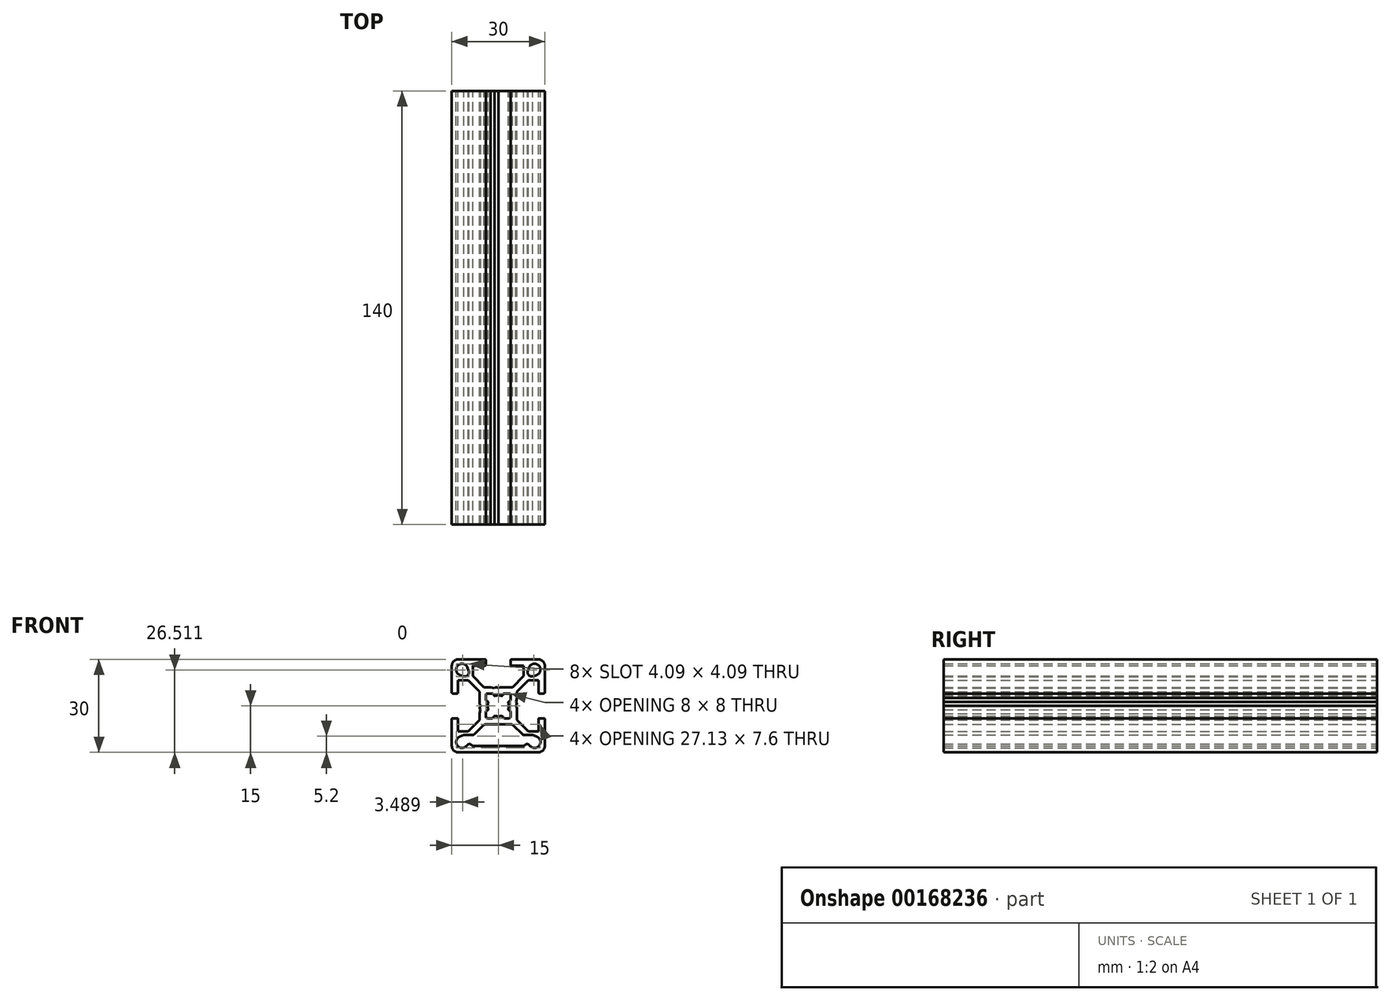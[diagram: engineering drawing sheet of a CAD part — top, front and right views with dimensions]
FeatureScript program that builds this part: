
annotation { "Feature Type Name" : "Feature", "Feature Type Description" : "" }
export const myFeature = defineFeature(function(context is Context, id is Id, definition is map)
    precondition{}
    {
        {
            var Q0;
            Q0=qCreatedBy(makeId("Front.planeOp"),FACE);
            var sketch = newSketch(context, id + "F0", { "sketchPlane" : qUnion([Q0])});
            skLineSegment(sketch, "E0", {"start": v(0, 17) * mm, "end": v(0, -17) * mm});
            skLineSegment(sketch, "E1", {"start": v(-17, 0) * mm, "end": v(17, 0) * mm});
            skLineSegment(sketch, "E2", {"start": v(-13, 15) * mm, "end": v(-4.3, 15) * mm});
            skLineSegment(sketch, "E3", {"start": v(-13, -15) * mm, "end": v(13, -15) * mm});
            skLineSegment(sketch, "E4", {"start": v(-15, 13) * mm, "end": v(-15, 4.3) * mm});
            skArc(sketch, "E5", {"start": v(15, 13) * mm, "mid": v(14.41, 14.41) * mm, "end": v(13, 15) * mm});
            skArc(sketch, "E6", {"start": v(-13, 15) * mm, "mid": v(-14.41, 14.41) * mm, "end": v(-15, 13) * mm});
            skArc(sketch, "E7", {"start": v(-15, -13) * mm, "mid": v(-14.41, -14.41) * mm, "end": v(-13, -15) * mm});
            skArc(sketch, "E8", {"start": v(13, -15) * mm, "mid": v(14.41, -14.41) * mm, "end": v(15, -13) * mm});
            skLineSegment(sketch, "E9", {"start": v(-13, -8.25) * mm, "end": v(-13, -4.3) * mm});
            skLineSegment(sketch, "E10", {"start": v(-8.08, -13) * mm, "end": v(8.08, -13) * mm});
            skLineSegment(sketch, "E11", {"start": v(-14.7, -4) * mm, "end": v(-13.3, -4) * mm});
            skLineSegment(sketch, "E12", {"start": v(-14.7, 4) * mm, "end": v(-13.3, 4) * mm});
            skLineSegment(sketch, "E13", {"start": v(-13, 4.3) * mm, "end": v(-13, 8.25) * mm});
            skLineSegment(sketch, "E14", {"start": v(4.3, 15) * mm, "end": v(13, 15) * mm});
            skLineSegment(sketch, "E15", {"start": v(-9.66, -8.25) * mm, "end": v(-13, -8.25) * mm});
            skLineSegment(sketch, "E16", {"start": v(-9.66, 8.25) * mm, "end": v(-13, 8.25) * mm});
            skLineSegment(sketch, "E17", {"start": v(4.59, 6) * mm, "end": v(0.65, 6) * mm});
            skLineSegment(sketch, "E18", {"start": v(4.17, -6) * mm, "end": v(-4.17, -6) * mm});
            skLineSegment(sketch, "E19", {"start": v(-6, -4.59) * mm, "end": v(-6, -2.5) * mm});
            skLineSegment(sketch, "E20", {"start": v(-4.59, 6) * mm, "end": v(-8.25, 9.66) * mm});
            skLineSegment(sketch, "E21", {"start": v(-6, 4.59) * mm, "end": v(-9.66, 8.25) * mm});
            skLineSegment(sketch, "E22", {"start": v(4.59, 6) * mm, "end": v(8.25, 9.66) * mm});
            skLineSegment(sketch, "E23", {"start": v(4.88, -6.3) * mm, "end": v(7.74, -9.16) * mm});
            skLineSegment(sketch, "E24", {"start": v(-4.88, -6.3) * mm, "end": v(-7.74, -9.16) * mm});
            skLineSegment(sketch, "E25", {"start": v(-6, -4.59) * mm, "end": v(-9.66, -8.25) * mm});
            skLineSegment(sketch, "E26", {"start": v(-15, -4.3) * mm, "end": v(-15, -13) * mm});
            skLineSegment(sketch, "E27", {"start": v(-4, 14.7) * mm, "end": v(-4, 13.3) * mm});
            skLineSegment(sketch, "E28", {"start": v(4, 14.7) * mm, "end": v(4, 13.3) * mm});
            skLineSegment(sketch, "E29", {"start": v(8.25, 9.66) * mm, "end": v(8.25, 13) * mm});
            skLineSegment(sketch, "E30", {"start": v(-8.25, 9.66) * mm, "end": v(-8.25, 13) * mm});
            skLineSegment(sketch, "E31", {"start": v(-4.3, 13) * mm, "end": v(-8.25, 13) * mm});
            skLineSegment(sketch, "E32", {"start": v(4.3, 13) * mm, "end": v(8.25, 13) * mm});
            skArc(sketch, "E33", {"start": v(-9.91, 12.35) * mm, "mid": v(-13.04, 13.04) * mm, "end": v(-12.35, 9.91) * mm});
            skLineSegment(sketch, "E34", {"start": v(-9.55, 11.34) * mm, "end": v(-9.91, 12.35) * mm});
            skLineSegment(sketch, "E35", {"start": v(-11.34, 9.55) * mm, "end": v(-12.35, 9.91) * mm});
            skArc(sketch, "E36", {"start": v(-11.34, 9.55) * mm, "mid": v(-9.87, 9.87) * mm, "end": v(-9.55, 11.34) * mm});
            skLineSegment(sketch, "E37", {"start": v(-8.45, -9.45) * mm, "end": v(-11.07, -9.45) * mm});
            skLineSegment(sketch, "E38", {"start": v(-11.07, -9.45) * mm, "end": v(-12.35, -9.91) * mm});
            skArc(sketch, "E39", {"start": v(-12.35, -9.91) * mm, "mid": v(-13.2, -12.86) * mm, "end": v(-10.14, -12.78) * mm});
            skArc(sketch, "E40", {"start": v(-8.5, -12.78) * mm, "mid": v(-9.31, -12.35) * mm, "end": v(-10.14, -12.78) * mm});
            skArc(sketch, "E41", {"start": v(-8.45, -9.45) * mm, "mid": v(-8.07, -9.37) * mm, "end": v(-7.74, -9.16) * mm});
            skArc(sketch, "E42", {"start": v(-4.17, -6) * mm, "mid": v(-4.55, -6.08) * mm, "end": v(-4.88, -6.3) * mm});
            skArc(sketch, "E43", {"start": v(4.88, -6.3) * mm, "mid": v(4.55, -6.08) * mm, "end": v(4.17, -6) * mm});
            skLineSegment(sketch, "E44", {"start": v(3.5, 4) * mm, "end": v(2, 4) * mm});
            skLineSegment(sketch, "E45", {"start": v(4, -3.5) * mm, "end": v(4, -2) * mm});
            skLineSegment(sketch, "E46", {"start": v(3.5, -4) * mm, "end": v(2, -4) * mm});
            skLineSegment(sketch, "E47", {"start": v(-4, -3.5) * mm, "end": v(-4, -2) * mm});
            skLineSegment(sketch, "E48", {"start": v(-2.5, 6) * mm, "end": v(-1.22, 5.75) * mm});
            skLineSegment(sketch, "E49", {"start": v(0, 5.7) * mm, "end": v(-0.4, 5.93) * mm});
            skLineSegment(sketch, "E50", {"start": v(0, 5.7) * mm, "end": v(0.4, 5.93) * mm});
            skLineSegment(sketch, "E51", {"start": v(-2.5, 6) * mm, "end": v(-4.59, 6) * mm});
            skArc(sketch, "E52", {"start": v(0.65, 6) * mm, "mid": v(0.52, 5.98) * mm, "end": v(0.4, 5.93) * mm});
            skArc(sketch, "E53", {"start": v(-0.4, 5.93) * mm, "mid": v(-0.65, 6) * mm, "end": v(-0.9, 5.93) * mm});
            skLineSegment(sketch, "E54", {"start": v(-1.22, 5.75) * mm, "end": v(-0.9, 5.93) * mm});
            skArc(sketch, "E55", {"start": v(-6, 0.65) * mm, "mid": v(-5.98, 0.52) * mm, "end": v(-5.93, 0.4) * mm});
            skLineSegment(sketch, "E56", {"start": v(-6, -2.5) * mm, "end": v(-5.75, -1.22) * mm});
            skLineSegment(sketch, "E57", {"start": v(-5.7, 0) * mm, "end": v(-5.93, -0.4) * mm});
            skLineSegment(sketch, "E58", {"start": v(-5.7, 0) * mm, "end": v(-5.93, 0.4) * mm});
            skArc(sketch, "E59", {"start": v(-5.93, -0.4) * mm, "mid": v(-6, -0.65) * mm, "end": v(-5.93, -0.9) * mm});
            skLineSegment(sketch, "E60", {"start": v(-5.75, -1.22) * mm, "end": v(-5.93, -0.9) * mm});
            skLineSegment(sketch, "E61", {"start": v(-6, 0.65) * mm, "end": v(-6, 4.59) * mm});
            skArc(sketch, "E62", {"start": v(4, 13.3) * mm, "mid": v(4.09, 13.09) * mm, "end": v(4.3, 13) * mm});
            skArc(sketch, "E63", {"start": v(4.3, 15) * mm, "mid": v(4.09, 14.91) * mm, "end": v(4, 14.7) * mm});
            skArc(sketch, "E64", {"start": v(-4.3, 13) * mm, "mid": v(-4.09, 13.09) * mm, "end": v(-4, 13.3) * mm});
            skArc(sketch, "E65", {"start": v(-4, 14.7) * mm, "mid": v(-4.09, 14.91) * mm, "end": v(-4.3, 15) * mm});
            skArc(sketch, "E66", {"start": v(-13.3, 4) * mm, "mid": v(-13.09, 4.09) * mm, "end": v(-13, 4.3) * mm});
            skArc(sketch, "E67", {"start": v(-15, 4.3) * mm, "mid": v(-14.91, 4.09) * mm, "end": v(-14.7, 4) * mm});
            skArc(sketch, "E68", {"start": v(-13, -4.3) * mm, "mid": v(-13.09, -4.09) * mm, "end": v(-13.3, -4) * mm});
            skArc(sketch, "E69", {"start": v(-14.7, -4) * mm, "mid": v(-14.91, -4.09) * mm, "end": v(-15, -4.3) * mm});
            skArc(sketch, "E70", {"start": v(0.99, 3.25) * mm, "mid": v(0, 3.4) * mm, "end": v(-0.99, 3.25) * mm});
            skArc(sketch, "E71", {"start": v(-1.5, 3.58) * mm, "mid": v(-1.32, 3.3) * mm, "end": v(-0.99, 3.25) * mm});
            skArc(sketch, "E72", {"start": v(-1.5, 3.58) * mm, "mid": v(-1.67, 3.88) * mm, "end": v(-2, 4) * mm});
            skArc(sketch, "E73", {"start": v(0.99, 3.25) * mm, "mid": v(1.32, 3.3) * mm, "end": v(1.5, 3.58) * mm});
            skArc(sketch, "E74", {"start": v(2, 4) * mm, "mid": v(1.67, 3.88) * mm, "end": v(1.5, 3.58) * mm});
            skLineSegment(sketch, "E75", {"start": v(-2, 4) * mm, "end": v(-3.5, 4) * mm});
            skArc(sketch, "E76", {"start": v(-3.5, 4) * mm, "mid": v(-3.85, 3.85) * mm, "end": v(-4, 3.5) * mm});
            skArc(sketch, "E77", {"start": v(4, 3.5) * mm, "mid": v(3.85, 3.85) * mm, "end": v(3.5, 4) * mm});
            skArc(sketch, "E78", {"start": v(3.5, -4) * mm, "mid": v(3.85, -3.85) * mm, "end": v(4, -3.5) * mm});
            skArc(sketch, "E79", {"start": v(-4, -3.5) * mm, "mid": v(-3.85, -3.85) * mm, "end": v(-3.5, -4) * mm});
            skArc(sketch, "E80", {"start": v(-3.25, 0.99) * mm, "mid": v(-3.4, 0) * mm, "end": v(-3.25, -0.99) * mm});
            skArc(sketch, "E81", {"start": v(-3.58, -1.5) * mm, "mid": v(-3.3, -1.32) * mm, "end": v(-3.25, -0.99) * mm});
            skArc(sketch, "E82", {"start": v(-3.58, -1.5) * mm, "mid": v(-3.88, -1.67) * mm, "end": v(-4, -2) * mm});
            skArc(sketch, "E83", {"start": v(-3.25, 0.99) * mm, "mid": v(-3.3, 1.32) * mm, "end": v(-3.58, 1.5) * mm});
            skArc(sketch, "E84", {"start": v(-4, 2) * mm, "mid": v(-3.88, 1.67) * mm, "end": v(-3.58, 1.5) * mm});
            skArc(sketch, "E85", {"start": v(3.25, -0.99) * mm, "mid": v(3.4, 0) * mm, "end": v(3.25, 0.99) * mm});
            skArc(sketch, "E86", {"start": v(3.58, 1.5) * mm, "mid": v(3.3, 1.32) * mm, "end": v(3.25, 0.99) * mm});
            skArc(sketch, "E87", {"start": v(3.58, 1.5) * mm, "mid": v(3.88, 1.67) * mm, "end": v(4, 2) * mm});
            skArc(sketch, "E88", {"start": v(3.25, -0.99) * mm, "mid": v(3.3, -1.32) * mm, "end": v(3.58, -1.5) * mm});
            skArc(sketch, "E89", {"start": v(4, -2) * mm, "mid": v(3.88, -1.67) * mm, "end": v(3.58, -1.5) * mm});
            skArc(sketch, "E90", {"start": v(-0.99, -3.25) * mm, "mid": v(0, -3.4) * mm, "end": v(0.99, -3.25) * mm});
            skArc(sketch, "E91", {"start": v(-0.99, -3.25) * mm, "mid": v(-1.32, -3.3) * mm, "end": v(-1.5, -3.58) * mm});
            skArc(sketch, "E92", {"start": v(-2, -4) * mm, "mid": v(-1.67, -3.88) * mm, "end": v(-1.5, -3.58) * mm});
            skArc(sketch, "E93", {"start": v(1.5, -3.58) * mm, "mid": v(1.32, -3.3) * mm, "end": v(0.99, -3.25) * mm});
            skArc(sketch, "E94", {"start": v(1.5, -3.58) * mm, "mid": v(1.67, -3.88) * mm, "end": v(2, -4) * mm});
            skLineSegment(sketch, "E95", {"start": v(4, 2) * mm, "end": v(4, 3.5) * mm});
            skLineSegment(sketch, "E96", {"start": v(-2, -4) * mm, "end": v(-3.5, -4) * mm});
            skLineSegment(sketch, "E97", {"start": v(-4, 2) * mm, "end": v(-4, 3.5) * mm});
            skCircle(sketch, "E98", {"center": v(0, 0) * mm, "radius": 3.4 * mm});
            skLineSegment(sketch, "E99", {"start": v(-11.7, -7.8) * mm, "end": v(-11.7, -15.6) * mm});
            skLineSegment(sketch, "E100", {"start": v(-15.6, -11.7) * mm, "end": v(-7.8, -11.7) * mm});
            skLineSegment(sketch, "E101", {"start": v(-11.7, 15.6) * mm, "end": v(-11.7, 7.8) * mm});
            skLineSegment(sketch, "E102", {"start": v(-15.6, 11.7) * mm, "end": v(-7.8, 11.7) * mm});
            skArc(sketch, "E103", {"start": v(7.74, -9.16) * mm, "mid": v(8.07, -9.37) * mm, "end": v(8.45, -9.45) * mm});
            skArc(sketch, "E104", {"start": v(12.35, 9.91) * mm, "mid": v(13.04, 13.04) * mm, "end": v(9.91, 12.35) * mm});
            skLineSegment(sketch, "E105", {"start": v(9.55, 11.34) * mm, "end": v(9.91, 12.35) * mm});
            skLineSegment(sketch, "E106", {"start": v(11.34, 9.55) * mm, "end": v(12.35, 9.91) * mm});
            skArc(sketch, "E107", {"start": v(9.55, 11.34) * mm, "mid": v(9.87, 9.87) * mm, "end": v(11.34, 9.55) * mm});
            skLineSegment(sketch, "E108", {"start": v(8.45, -9.45) * mm, "end": v(11.07, -9.45) * mm});
            skLineSegment(sketch, "E109", {"start": v(11.07, -9.45) * mm, "end": v(12.35, -9.91) * mm});
            skArc(sketch, "E110", {"start": v(10.14, -12.78) * mm, "mid": v(13.2, -12.86) * mm, "end": v(12.35, -9.91) * mm});
            skArc(sketch, "E111", {"start": v(10.14, -12.78) * mm, "mid": v(9.31, -12.35) * mm, "end": v(8.5, -12.78) * mm});
            skLineSegment(sketch, "E112", {"start": v(11.7, -7.8) * mm, "end": v(11.7, -15.6) * mm});
            skLineSegment(sketch, "E113", {"start": v(15.6, -11.7) * mm, "end": v(7.8, -11.7) * mm});
            skLineSegment(sketch, "E114", {"start": v(11.7, 15.6) * mm, "end": v(11.7, 7.8) * mm});
            skLineSegment(sketch, "E115", {"start": v(15.6, 11.7) * mm, "end": v(7.8, 11.7) * mm});
            skLineSegment(sketch, "E116", {"start": v(15, 13) * mm, "end": v(15, 4.3) * mm});
            skLineSegment(sketch, "E117", {"start": v(15, -4.3) * mm, "end": v(15, -13) * mm});
            skLineSegment(sketch, "E118", {"start": v(13, -8.25) * mm, "end": v(13, -4.3) * mm});
            skLineSegment(sketch, "E119", {"start": v(13, 4.3) * mm, "end": v(13, 8.25) * mm});
            skLineSegment(sketch, "E120", {"start": v(14.7, -4) * mm, "end": v(13.3, -4) * mm});
            skArc(sketch, "E121", {"start": v(13.3, -4) * mm, "mid": v(13.09, -4.09) * mm, "end": v(13, -4.3) * mm});
            skLineSegment(sketch, "E122", {"start": v(14.7, 4) * mm, "end": v(13.3, 4) * mm});
            skArc(sketch, "E123", {"start": v(14.7, 4) * mm, "mid": v(14.91, 4.09) * mm, "end": v(15, 4.3) * mm});
            skArc(sketch, "E124", {"start": v(13, 4.3) * mm, "mid": v(13.09, 4.09) * mm, "end": v(13.3, 4) * mm});
            skLineSegment(sketch, "E125", {"start": v(9.66, 8.25) * mm, "end": v(13, 8.25) * mm});
            skLineSegment(sketch, "E126", {"start": v(9.66, -8.25) * mm, "end": v(13, -8.25) * mm});
            skLineSegment(sketch, "E127", {"start": v(6, 4.59) * mm, "end": v(9.66, 8.25) * mm});
            skLineSegment(sketch, "E128", {"start": v(6, -4.59) * mm, "end": v(9.66, -8.25) * mm});
            skArc(sketch, "E129", {"start": v(15, -4.3) * mm, "mid": v(14.91, -4.09) * mm, "end": v(14.7, -4) * mm});
            skLineSegment(sketch, "E130", {"start": v(6, 4.59) * mm, "end": v(6, 2.5) * mm});
            skLineSegment(sketch, "E131", {"start": v(6, -0.65) * mm, "end": v(6, -4.59) * mm});
            skArc(sketch, "E132", {"start": v(6, -0.65) * mm, "mid": v(5.98, -0.52) * mm, "end": v(5.93, -0.4) * mm});
            skLineSegment(sketch, "E133", {"start": v(6, 2.5) * mm, "end": v(5.75, 1.22) * mm});
            skLineSegment(sketch, "E134", {"start": v(5.7, 0) * mm, "end": v(5.93, 0.4) * mm});
            skLineSegment(sketch, "E135", {"start": v(5.7, 0) * mm, "end": v(5.93, -0.4) * mm});
            skArc(sketch, "E136", {"start": v(5.93, 0.4) * mm, "mid": v(6, 0.65) * mm, "end": v(5.93, 0.9) * mm});
            skLineSegment(sketch, "E137", {"start": v(5.75, 1.22) * mm, "end": v(5.93, 0.9) * mm});
            skArc(sketch, "E138", {"start": v(8.08, -13) * mm, "mid": v(8.31, -12.94) * mm, "end": v(8.5, -12.78) * mm});
            skArc(sketch, "E139", {"start": v(-8.5, -12.78) * mm, "mid": v(-8.31, -12.94) * mm, "end": v(-8.08, -13) * mm});
            skSolve(sketch);
        }
        {
            var Q0;
            Q0=qCreatedBy(makeId("Front.planeOp"),FACE);
            var sketch = newSketch(context, id + "F1", { "sketchPlane" : qUnion([Q0])});
            skLineSegment(sketch, "E140.0", {"start": v(4.59, 6) * mm, "end": v(0.65, 6) * mm});
            skLineSegment(sketch, "E140.2", {"start": v(6, 4.59) * mm, "end": v(6, 2.5) * mm});
            skLineSegment(sketch, "E140.5", {"start": v(6, -0.65) * mm, "end": v(6, -4.59) * mm});
            skLineSegment(sketch, "E140.7", {"start": v(4.3, 13) * mm, "end": v(8.25, 13) * mm});
            skLineSegment(sketch, "E140.8", {"start": v(-15, 13) * mm, "end": v(-15, 4.3) * mm});
            skLineSegment(sketch, "E140.11", {"start": v(6, -4.59) * mm, "end": v(9.66, -8.25) * mm});
            skArc(sketch, "E140.12", {"start": v(-9.91, 12.35) * mm, "mid": v(-13.04, 13.04) * mm, "end": v(-12.35, 9.91) * mm});
            skLineSegment(sketch, "E140.13", {"start": v(4.17, -6) * mm, "end": v(-4.17, -6) * mm});
            skLineSegment(sketch, "E140.14", {"start": v(-2.5, 6) * mm, "end": v(-4.59, 6) * mm});
            skArc(sketch, "E140.15", {"start": v(15, 13) * mm, "mid": v(14.41, 14.41) * mm, "end": v(13, 15) * mm});
            skLineSegment(sketch, "E140.16", {"start": v(-8.08, -13) * mm, "end": v(8.08, -13) * mm});
            skLineSegment(sketch, "E140.17", {"start": v(-13, -8.25) * mm, "end": v(-13, -4.3) * mm});
            skArc(sketch, "E140.18", {"start": v(-15, -13) * mm, "mid": v(-14.41, -14.41) * mm, "end": v(-13, -15) * mm});
            skArc(sketch, "E140.19", {"start": v(13, -15) * mm, "mid": v(14.41, -14.41) * mm, "end": v(15, -13) * mm});
            skArc(sketch, "E140.20", {"start": v(-13, 15) * mm, "mid": v(-14.41, 14.41) * mm, "end": v(-15, 13) * mm});
            skLineSegment(sketch, "E140.21", {"start": v(15, 13) * mm, "end": v(15, 4.3) * mm});
            skLineSegment(sketch, "E140.22", {"start": v(-13, 15) * mm, "end": v(-4.3, 15) * mm});
            skLineSegment(sketch, "E140.23", {"start": v(-13, -15) * mm, "end": v(13, -15) * mm});
            skLineSegment(sketch, "E140.26", {"start": v(-9.66, -8.25) * mm, "end": v(-13, -8.25) * mm});
            skLineSegment(sketch, "E140.27", {"start": v(4.3, 15) * mm, "end": v(13, 15) * mm});
            skLineSegment(sketch, "E140.28", {"start": v(-4.3, 13) * mm, "end": v(-8.25, 13) * mm});
            skLineSegment(sketch, "E140.29", {"start": v(6, 4.59) * mm, "end": v(9.66, 8.25) * mm});
            skLineSegment(sketch, "E140.30", {"start": v(-13, 4.3) * mm, "end": v(-13, 8.25) * mm});
            skLineSegment(sketch, "E140.31", {"start": v(-6, -4.59) * mm, "end": v(-6, -2.5) * mm});
            skArc(sketch, "E140.32", {"start": v(-11.34, 9.55) * mm, "mid": v(-9.87, 9.87) * mm, "end": v(-9.55, 11.34) * mm});
            skArc(sketch, "E140.33", {"start": v(10.14, -12.78) * mm, "mid": v(13.2, -12.86) * mm, "end": v(12.35, -9.91) * mm});
            skLineSegment(sketch, "E140.34", {"start": v(8.45, -9.45) * mm, "end": v(11.07, -9.45) * mm});
            skLineSegment(sketch, "E140.35", {"start": v(-8.25, 9.66) * mm, "end": v(-8.25, 13) * mm});
            skLineSegment(sketch, "E140.36", {"start": v(9.66, -8.25) * mm, "end": v(13, -8.25) * mm});
            skLineSegment(sketch, "E140.37", {"start": v(8.25, 9.66) * mm, "end": v(8.25, 13) * mm});
            skLineSegment(sketch, "E140.38", {"start": v(-6, 0.65) * mm, "end": v(-6, 4.59) * mm});
            skArc(sketch, "E140.39", {"start": v(9.55, 11.34) * mm, "mid": v(9.87, 9.87) * mm, "end": v(11.34, 9.55) * mm});
            skLineSegment(sketch, "E140.40", {"start": v(9.66, 8.25) * mm, "end": v(13, 8.25) * mm});
            skLineSegment(sketch, "E140.41", {"start": v(-4.59, 6) * mm, "end": v(-8.25, 9.66) * mm});
            skLineSegment(sketch, "E140.42", {"start": v(-15, -4.3) * mm, "end": v(-15, -13) * mm});
            skLineSegment(sketch, "E140.43", {"start": v(-6, -4.59) * mm, "end": v(-9.66, -8.25) * mm});
            skArc(sketch, "E140.44", {"start": v(12.35, 9.91) * mm, "mid": v(13.04, 13.04) * mm, "end": v(9.91, 12.35) * mm});
            skLineSegment(sketch, "E140.45", {"start": v(-4.88, -6.3) * mm, "end": v(-7.74, -9.16) * mm});
            skLineSegment(sketch, "E140.46", {"start": v(13, -8.25) * mm, "end": v(13, -4.3) * mm});
            skArc(sketch, "E140.48", {"start": v(-12.35, -9.91) * mm, "mid": v(-13.2, -12.86) * mm, "end": v(-10.14, -12.78) * mm});
            skLineSegment(sketch, "E140.49", {"start": v(13, 4.3) * mm, "end": v(13, 8.25) * mm});
            skLineSegment(sketch, "E140.50", {"start": v(4.88, -6.3) * mm, "end": v(7.74, -9.16) * mm});
            skLineSegment(sketch, "E140.51", {"start": v(4.59, 6) * mm, "end": v(8.25, 9.66) * mm});
            skLineSegment(sketch, "E140.52", {"start": v(-8.45, -9.45) * mm, "end": v(-11.07, -9.45) * mm});
            skLineSegment(sketch, "E140.53", {"start": v(-6, 4.59) * mm, "end": v(-9.66, 8.25) * mm});
            skLineSegment(sketch, "E140.54", {"start": v(15, -4.3) * mm, "end": v(15, -13) * mm});
            skLineSegment(sketch, "E140.57", {"start": v(-9.66, 8.25) * mm, "end": v(-13, 8.25) * mm});
            skArc(sketch, "E140.58", {"start": v(-0.99, -3.25) * mm, "mid": v(0, -3.4) * mm, "end": v(0.99, -3.25) * mm});
            skArc(sketch, "E140.59", {"start": v(0.99, 3.25) * mm, "mid": v(0, 3.4) * mm, "end": v(-0.99, 3.25) * mm});
            skLineSegment(sketch, "E140.60", {"start": v(-11.34, 9.55) * mm, "end": v(-12.35, 9.91) * mm});
            skArc(sketch, "E140.61", {"start": v(-3.58, -1.5) * mm, "mid": v(-3.3, -1.32) * mm, "end": v(-3.25, -0.99) * mm});
            skLineSegment(sketch, "E140.62", {"start": v(-9.55, 11.34) * mm, "end": v(-9.91, 12.35) * mm});
            skLineSegment(sketch, "E140.63", {"start": v(-2.5, 6) * mm, "end": v(-1.22, 5.75) * mm});
            skLineSegment(sketch, "E140.64", {"start": v(-2, -4) * mm, "end": v(-3.5, -4) * mm});
            skLineSegment(sketch, "E140.65", {"start": v(-4, 2) * mm, "end": v(-4, 3.5) * mm});
            skArc(sketch, "E140.66", {"start": v(-3.25, 0.99) * mm, "mid": v(-3.4, 0) * mm, "end": v(-3.25, -0.99) * mm});
            skArc(sketch, "E140.67", {"start": v(-3.58, -1.5) * mm, "mid": v(-3.88, -1.67) * mm, "end": v(-4, -2) * mm});
            skLineSegment(sketch, "E140.68", {"start": v(4, 2) * mm, "end": v(4, 3.5) * mm});
            skArc(sketch, "E140.69", {"start": v(6, -0.65) * mm, "mid": v(5.98, -0.52) * mm, "end": v(5.93, -0.4) * mm});
            skArc(sketch, "E140.70", {"start": v(10.14, -12.78) * mm, "mid": v(9.31, -12.35) * mm, "end": v(8.5, -12.78) * mm});
            skArc(sketch, "E140.71", {"start": v(-4, -3.5) * mm, "mid": v(-3.85, -3.85) * mm, "end": v(-3.5, -4) * mm});
            skLineSegment(sketch, "E140.72", {"start": v(-4, -3.5) * mm, "end": v(-4, -2) * mm});
            skArc(sketch, "E140.73", {"start": v(1.5, -3.58) * mm, "mid": v(1.67, -3.88) * mm, "end": v(2, -4) * mm});
            skLineSegment(sketch, "E140.74", {"start": v(3.5, 4) * mm, "end": v(2, 4) * mm});
            skLineSegment(sketch, "E140.75", {"start": v(3.5, -4) * mm, "end": v(2, -4) * mm});
            skArc(sketch, "E140.76", {"start": v(3.5, -4) * mm, "mid": v(3.85, -3.85) * mm, "end": v(4, -3.5) * mm});
            skArc(sketch, "E140.77", {"start": v(-3.5, 4) * mm, "mid": v(-3.85, 3.85) * mm, "end": v(-4, 3.5) * mm});
            skLineSegment(sketch, "E140.78", {"start": v(4, -3.5) * mm, "end": v(4, -2) * mm});
            skArc(sketch, "E140.79", {"start": v(4, 3.5) * mm, "mid": v(3.85, 3.85) * mm, "end": v(3.5, 4) * mm});
            skLineSegment(sketch, "E140.80", {"start": v(-2, 4) * mm, "end": v(-3.5, 4) * mm});
            skArc(sketch, "E140.81", {"start": v(-8.5, -12.78) * mm, "mid": v(-8.31, -12.94) * mm, "end": v(-8.08, -13) * mm});
            skLineSegment(sketch, "E140.82", {"start": v(11.07, -9.45) * mm, "end": v(12.35, -9.91) * mm});
            skArc(sketch, "E140.83", {"start": v(4.88, -6.3) * mm, "mid": v(4.55, -6.08) * mm, "end": v(4.17, -6) * mm});
            skArc(sketch, "E140.84", {"start": v(8.08, -13) * mm, "mid": v(8.31, -12.94) * mm, "end": v(8.5, -12.78) * mm});
            skArc(sketch, "E140.85", {"start": v(-4, 2) * mm, "mid": v(-3.88, 1.67) * mm, "end": v(-3.58, 1.5) * mm});
            skArc(sketch, "E140.86", {"start": v(-4.17, -6) * mm, "mid": v(-4.55, -6.08) * mm, "end": v(-4.88, -6.3) * mm});
            skLineSegment(sketch, "E140.87", {"start": v(11.34, 9.55) * mm, "end": v(12.35, 9.91) * mm});
            skArc(sketch, "E140.88", {"start": v(-8.45, -9.45) * mm, "mid": v(-8.07, -9.37) * mm, "end": v(-7.74, -9.16) * mm});
            skLineSegment(sketch, "E140.89", {"start": v(9.55, 11.34) * mm, "end": v(9.91, 12.35) * mm});
            skArc(sketch, "E140.90", {"start": v(4, -2) * mm, "mid": v(3.88, -1.67) * mm, "end": v(3.58, -1.5) * mm});
            skArc(sketch, "E140.91", {"start": v(-1.5, 3.58) * mm, "mid": v(-1.67, 3.88) * mm, "end": v(-2, 4) * mm});
            skArc(sketch, "E140.92", {"start": v(-8.5, -12.78) * mm, "mid": v(-9.31, -12.35) * mm, "end": v(-10.14, -12.78) * mm});
            skArc(sketch, "E140.93", {"start": v(3.25, -0.99) * mm, "mid": v(3.3, -1.32) * mm, "end": v(3.58, -1.5) * mm});
            skLineSegment(sketch, "E140.94", {"start": v(-6, -2.5) * mm, "end": v(-5.75, -1.22) * mm});
            skArc(sketch, "E140.95", {"start": v(-1.5, 3.58) * mm, "mid": v(-1.32, 3.3) * mm, "end": v(-0.99, 3.25) * mm});
            skLineSegment(sketch, "E140.96", {"start": v(-11.07, -9.45) * mm, "end": v(-12.35, -9.91) * mm});
            skArc(sketch, "E140.97", {"start": v(7.74, -9.16) * mm, "mid": v(8.07, -9.37) * mm, "end": v(8.45, -9.45) * mm});
            skArc(sketch, "E140.98", {"start": v(3.58, 1.5) * mm, "mid": v(3.88, 1.67) * mm, "end": v(4, 2) * mm});
            skArc(sketch, "E140.99", {"start": v(3.58, 1.5) * mm, "mid": v(3.3, 1.32) * mm, "end": v(3.25, 0.99) * mm});
            skArc(sketch, "E140.100", {"start": v(3.25, -0.99) * mm, "mid": v(3.4, 0) * mm, "end": v(3.25, 0.99) * mm});
            skLineSegment(sketch, "E140.101", {"start": v(6, 2.5) * mm, "end": v(5.75, 1.22) * mm});
            skArc(sketch, "E140.102", {"start": v(15, -4.3) * mm, "mid": v(14.91, -4.09) * mm, "end": v(14.7, -4) * mm});
            skArc(sketch, "E140.103", {"start": v(-15, 4.3) * mm, "mid": v(-14.91, 4.09) * mm, "end": v(-14.7, 4) * mm});
            skLineSegment(sketch, "E140.104", {"start": v(-14.7, 4) * mm, "end": v(-13.3, 4) * mm});
            skLineSegment(sketch, "E140.105", {"start": v(0, 5.7) * mm, "end": v(-0.4, 5.93) * mm});
            skLineSegment(sketch, "E140.106", {"start": v(0, 5.7) * mm, "end": v(0.4, 5.93) * mm});
            skArc(sketch, "E140.107", {"start": v(-4, 14.7) * mm, "mid": v(-4.09, 14.91) * mm, "end": v(-4.3, 15) * mm});
            skArc(sketch, "E140.108", {"start": v(-13.3, 4) * mm, "mid": v(-13.09, 4.09) * mm, "end": v(-13, 4.3) * mm});
            skLineSegment(sketch, "E140.109", {"start": v(-14.7, -4) * mm, "end": v(-13.3, -4) * mm});
            skArc(sketch, "E140.110", {"start": v(-3.25, 0.99) * mm, "mid": v(-3.3, 1.32) * mm, "end": v(-3.58, 1.5) * mm});
            skArc(sketch, "E140.111", {"start": v(13, 4.3) * mm, "mid": v(13.09, 4.09) * mm, "end": v(13.3, 4) * mm});
            skArc(sketch, "E140.112", {"start": v(-2, -4) * mm, "mid": v(-1.67, -3.88) * mm, "end": v(-1.5, -3.58) * mm});
            skArc(sketch, "E140.113", {"start": v(14.7, 4) * mm, "mid": v(14.91, 4.09) * mm, "end": v(15, 4.3) * mm});
            skArc(sketch, "E140.114", {"start": v(-0.99, -3.25) * mm, "mid": v(-1.32, -3.3) * mm, "end": v(-1.5, -3.58) * mm});
            skArc(sketch, "E140.115", {"start": v(1.5, -3.58) * mm, "mid": v(1.32, -3.3) * mm, "end": v(0.99, -3.25) * mm});
            skArc(sketch, "E140.116", {"start": v(2, 4) * mm, "mid": v(1.67, 3.88) * mm, "end": v(1.5, 3.58) * mm});
            skArc(sketch, "E140.117", {"start": v(-13, -4.3) * mm, "mid": v(-13.09, -4.09) * mm, "end": v(-13.3, -4) * mm});
            skLineSegment(sketch, "E140.118", {"start": v(14.7, 4) * mm, "end": v(13.3, 4) * mm});
            skLineSegment(sketch, "E140.119", {"start": v(5.75, 1.22) * mm, "end": v(5.93, 0.9) * mm});
            skArc(sketch, "E140.120", {"start": v(0.99, 3.25) * mm, "mid": v(1.32, 3.3) * mm, "end": v(1.5, 3.58) * mm});
            skArc(sketch, "E140.121", {"start": v(13.3, -4) * mm, "mid": v(13.09, -4.09) * mm, "end": v(13, -4.3) * mm});
            skArc(sketch, "E140.122", {"start": v(5.93, 0.4) * mm, "mid": v(6, 0.65) * mm, "end": v(5.93, 0.9) * mm});
            skLineSegment(sketch, "E140.123", {"start": v(14.7, -4) * mm, "end": v(13.3, -4) * mm});
            skLineSegment(sketch, "E140.124", {"start": v(5.7, 0) * mm, "end": v(5.93, -0.4) * mm});
            skLineSegment(sketch, "E140.125", {"start": v(5.7, 0) * mm, "end": v(5.93, 0.4) * mm});
            skLineSegment(sketch, "E140.126", {"start": v(-1.22, 5.75) * mm, "end": v(-0.9, 5.93) * mm});
            skArc(sketch, "E140.127", {"start": v(-14.7, -4) * mm, "mid": v(-14.91, -4.09) * mm, "end": v(-15, -4.3) * mm});
            skArc(sketch, "E140.128", {"start": v(-4.3, 13) * mm, "mid": v(-4.09, 13.09) * mm, "end": v(-4, 13.3) * mm});
            skArc(sketch, "E140.129", {"start": v(4.3, 15) * mm, "mid": v(4.09, 14.91) * mm, "end": v(4, 14.7) * mm});
            skLineSegment(sketch, "E140.130", {"start": v(4, 14.7) * mm, "end": v(4, 13.3) * mm});
            skArc(sketch, "E140.131", {"start": v(4, 13.3) * mm, "mid": v(4.09, 13.09) * mm, "end": v(4.3, 13) * mm});
            skLineSegment(sketch, "E140.132", {"start": v(-4, 14.7) * mm, "end": v(-4, 13.3) * mm});
            skArc(sketch, "E140.133", {"start": v(0.65, 6) * mm, "mid": v(0.52, 5.98) * mm, "end": v(0.4, 5.93) * mm});
            skArc(sketch, "E140.134", {"start": v(-0.4, 5.93) * mm, "mid": v(-0.65, 6) * mm, "end": v(-0.9, 5.93) * mm});
            skLineSegment(sketch, "E140.135", {"start": v(-5.75, -1.22) * mm, "end": v(-5.93, -0.9) * mm});
            skArc(sketch, "E140.136", {"start": v(-5.93, -0.4) * mm, "mid": v(-6, -0.65) * mm, "end": v(-5.93, -0.9) * mm});
            skLineSegment(sketch, "E140.137", {"start": v(-5.7, 0) * mm, "end": v(-5.93, 0.4) * mm});
            skArc(sketch, "E140.138", {"start": v(-6, 0.65) * mm, "mid": v(-5.98, 0.52) * mm, "end": v(-5.93, 0.4) * mm});
            skLineSegment(sketch, "E140.139", {"start": v(-5.7, 0) * mm, "end": v(-5.93, -0.4) * mm});
            skSolve(sketch);
        }
        {
            var Q0;
            Q0=makeQuery(id+"F1.imprint","IMPRINT",FACE,{"disambiguationData":[TD([[makeQuery(id+"F1.imprint","IMPRINT",EDGE,{"derivedFrom":sQuery(id+"F1.wireOp",EDGE,"E140.0")}),1.0]])]});
            extrude(context, id + "F2", {"entities" : qUnion([Q0]), "endBound" : BoundingType.SYMMETRIC, "depth" : 140 * mm});
        }
    });
